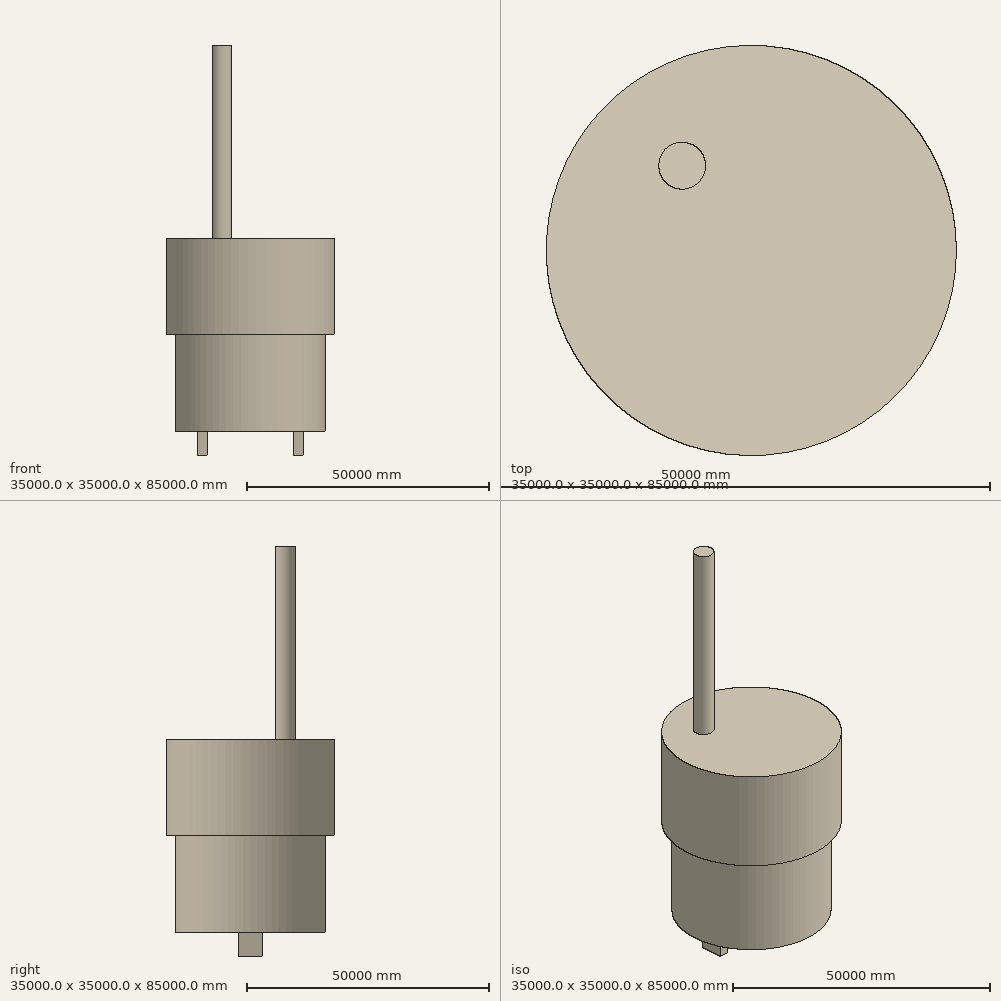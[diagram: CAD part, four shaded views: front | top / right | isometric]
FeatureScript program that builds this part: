
annotation { "Feature Type Name" : "Feature", "Feature Type Description" : "" }
export const myFeature = defineFeature(function(context is Context, id is Id, definition is map)
    precondition{}
    {
        {
            var Q0;
            Q0=qCreatedBy(makeId("Top.planeOp"),FACE);
            var sketch = newSketch(context, id + "F0", { "sketchPlane" : qUnion([Q0])});
            skCircle(sketch, "E0", {"center": v(0, 0) * mm, "radius": 15500 * mm});
            skCircle(sketch, "E1", {"center": v(0, 0) * mm, "radius": 17500 * mm});
            skSolve(sketch);
        }
        {
            var Q0;
            Q0=makeQuery(id+"F0.imprint","IMPRINT",FACE,{"disambiguationData":[TD([[makeQuery(id+"F0.imprint","IMPRINT",EDGE,{"derivedFrom":sQuery(id+"F0.wireOp",EDGE,"E0")}),1.0]])]});
            var Q1;
            Q1=sQuery(id+"F0.wireOp",EDGE,"E0");
            extrude(context, id + "F1", {"entities" : qUnion([Q0]), "surfaceEntities" : qUnion([Q1]), "oppositeDirection" : true, "depth" : 20000 * mm, "offsetDistance" : 25 * mm});
        }
        {
            var Q0;
            Q0=makeQuery(id+"F0.imprint","IMPRINT",FACE,{"disambiguationData":[TD([[makeQuery(id+"F0.imprint","IMPRINT",EDGE,{"derivedFrom":sQuery(id+"F0.wireOp",EDGE,"E0")}),-1.0]])]});
            var Q1;
            Q1=makeQuery(id+"F0.imprint","IMPRINT",FACE,{"disambiguationData":[TD([[makeQuery(id+"F0.imprint","IMPRINT",EDGE,{"derivedFrom":sQuery(id+"F0.wireOp",EDGE,"E0")}),1.0]])]});
            var Q2;
            Q2=sQuery(id+"F0.wireOp",EDGE,"E1");
            extrude(context, id + "F2", {"entities" : qUnion([Q0, Q1]), "surfaceEntities" : qUnion([Q2]), "depth" : 20000 * mm, "offsetDistance" : 25 * mm});
        }
        {
            var Q0;
            Q0=makeQuery(id+"F2.opExtrude","CAP_FACE",FACE,{"disambiguationData":[OSD([sQuery(id+"F0.wireOp",EDGE,"E1")])],"isStart":false});
            var sketch = newSketch(context, id + "F3", { "sketchPlane" : qUnion([Q0])});
            skCircle(sketch, "E2", {"center": v(-5896.74, 7228.26) * mm, "radius": 2000 * mm});
            skSolve(sketch);
        }
        {
            var Q0;
            Q0 = qSketchRegion(id + "F3", true);
            extrude(context, id + "F4", {"entities" : qUnion([Q0]), "operationType" : NewBodyOperationType.ADD, "depth" : 40000 * mm, "offsetDistance" : 25 * mm});
        }
        {
            var Q0;
            Q0=makeQuery(id+"F1.opExtrude","CAP_FACE",FACE,{"disambiguationData":[OSD([sQuery(id+"F0.wireOp",EDGE,"E0")])],"isStart":false});
            var sketch = newSketch(context, id + "F5", { "sketchPlane" : qUnion([Q0])});
            skLineSegment(sketch, "E3.bottom", {"start": v(-11000, 2420.65) * mm, "end": v(-9000, 2420.65) * mm});
            skLineSegment(sketch, "E3.top", {"start": v(-11000, -2579.35) * mm, "end": v(-9000, -2579.35) * mm});
            skLineSegment(sketch, "E3.left", {"start": v(-11000, 2420.65) * mm, "end": v(-11000, -2579.35) * mm});
            skLineSegment(sketch, "E3.right", {"start": v(-9000, 2420.65) * mm, "end": v(-9000, -2579.35) * mm});
            skLineSegment(sketch, "E4.bottom", {"start": v(9000, 2465.57) * mm, "end": v(11000, 2465.57) * mm});
            skLineSegment(sketch, "E4.top", {"start": v(9000, -2534.43) * mm, "end": v(11000, -2534.43) * mm});
            skLineSegment(sketch, "E4.left", {"start": v(9000, 2465.57) * mm, "end": v(9000, -2534.43) * mm});
            skLineSegment(sketch, "E4.right", {"start": v(11000, 2465.57) * mm, "end": v(11000, -2534.43) * mm});
            skSolve(sketch);
        }
        {
            var Q0;
            Q0=makeQuery(id+"F5.imprint","IMPRINT",FACE,{"disambiguationData":[TD([[makeQuery(id+"F5.imprint","IMPRINT",EDGE,{"derivedFrom":sQuery(id+"F5.wireOp",EDGE,"E3.bottom")}),-1.0]])]});
            var Q1;
            Q1=makeQuery(id+"F5.imprint","IMPRINT",FACE,{"disambiguationData":[TD([[makeQuery(id+"F5.imprint","IMPRINT",EDGE,{"derivedFrom":sQuery(id+"F5.wireOp",EDGE,"E4.bottom")}),-1.0]])]});
            extrude(context, id + "F6", {"entities" : qUnion([Q0, Q1]), "operationType" : NewBodyOperationType.ADD, "depth" : 5000 * mm, "offsetDistance" : 25 * mm});
        }
    });
